# Revit family: Doors_Industrial_Wayne-Dalton_Insulated-Sectional-Steel-Doors-ThermoMark-Model-5155_
name_source: partatom
category: Specialty Equipment
units: mm (PartAtom-declared; Revit-internal decimal feet)

## family parameters
Always vertical = Yes
Cut with Voids When Loaded = No
Host = Wall
OmniClass Number = 23.30.10.21.34
OmniClass Title = Industrial Doors
Part Type = Normal
Room Calculation Point = No
Round Connector Dimension = Use Diameter
Shared = No

## types (5) — shared parameters
Array Offset = 0' - 0"
Description = Model 5155 foamed in place insulated steel door, 1-1/2" thick, U-factor .15 R-Vlaue 12.12.
End Stile (Width) = 0' - 3 5/16"
Manufacturer = Wayne Dalton
Model = 5155
Power Factor = 1
Product Guid = 909fb480-90cf-4c9c-818d-730314a3d302
Product Page URL = https://www.wayne-dalton.com
Product data url = https://www.bimobject.com
URL = https://www.wayne-dalton.com
Wall Closure = By host

## per-type parameters (varying)
| type | Apparent Load Phase 1 | Apparent Load Phase 2 | Apparent Load Phase 3 | Array Count | Current | Frequency | Number of Poles | Voltage |
| 115 volts, one phase, 60 Hz (110-120V range) | 2300 VA | 0 VA | 0 VA | 3 | 20 A | 60 Hz | 1 | 115 V |
| 230 volts, single phase, 60 Hz (208-245V range) | 4600 VA | 0 VA | 0 VA | 3 | 20 A | 60 Hz | 1 | 230 V |
| 230 volts, three phase, 60 Hz (208-245V range) | 2656 VA | 2656 VA | 2656 VA | 3 | 20 A | 60 Hz | 3 | 230 V |
| 460 volts, three phase, 60 Hz (456-495V range) | 3984 VA | 3984 VA | 3984 VA | 3 | 15 A | 60 Hz | 3 | 460 V |
| Chain Hoist | 0 VA | 0 VA | 0 VA | 2 | 0 A | 0 Hz | 1 | 0 V |

type visibility flags (boolean, named after types; folded from table):
- 115 volts, one phase, 60 Hz (110-120V range): Yes: (none)
- 230 volts, single phase, 60 Hz (208-245V range): Yes: (none)
- 230 volts, three phase, 60 Hz (208-245V range): Yes: (none)
- 460 volts, three phase, 60 Hz (456-495V range): Yes: (none)
- Chain Hoist: Yes: Chain Hoist

## geometry (parser evidence)
native form markers: Sweep x13
no freeform markers — native parametric forms only
